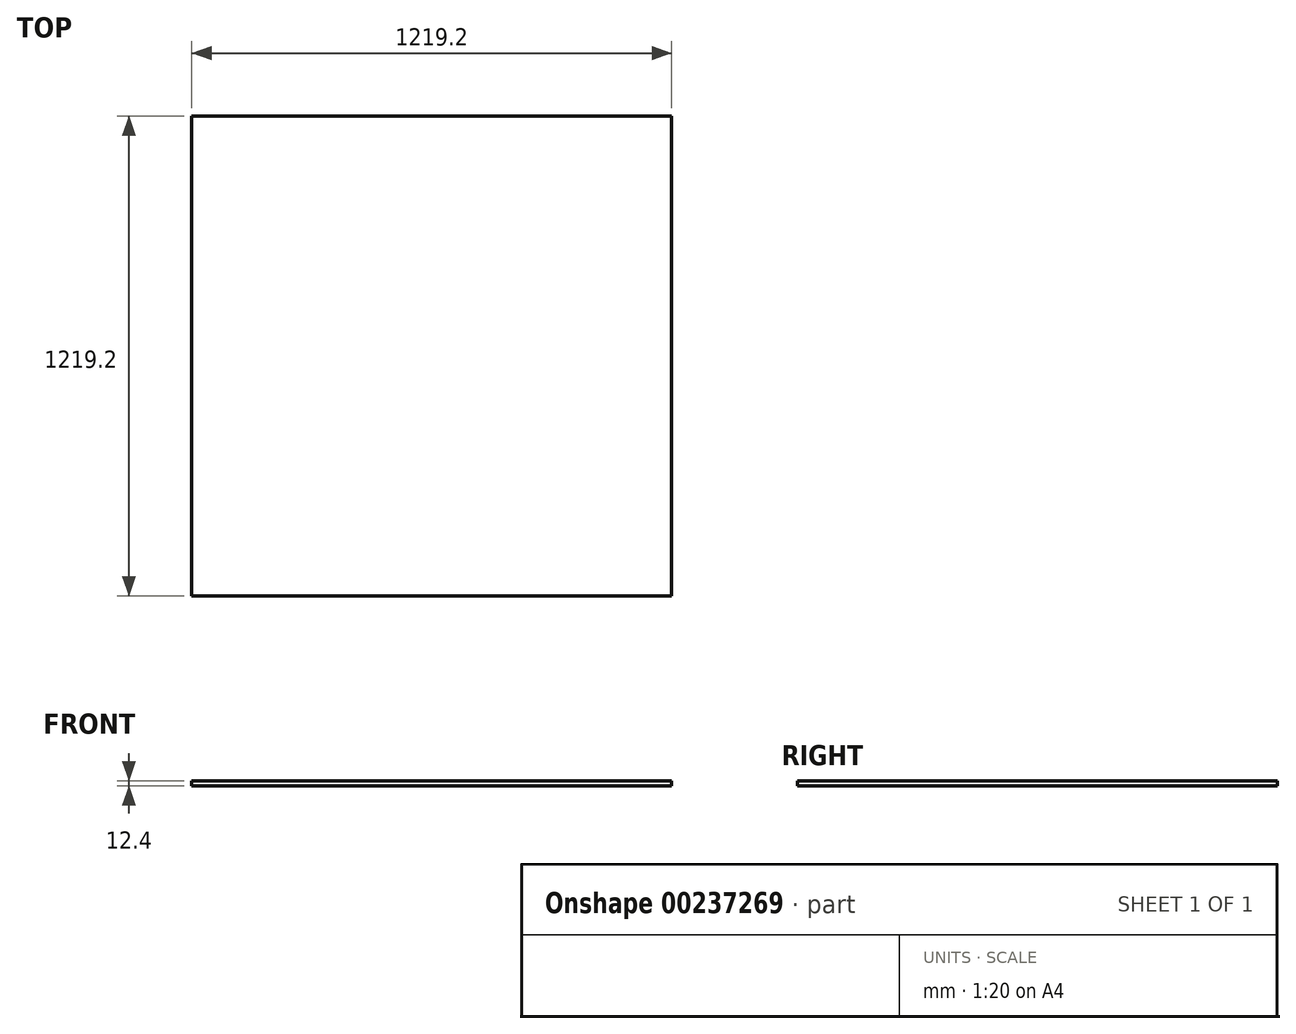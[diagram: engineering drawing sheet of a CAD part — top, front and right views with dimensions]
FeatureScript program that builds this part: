
annotation { "Feature Type Name" : "Feature", "Feature Type Description" : "" }
export const myFeature = defineFeature(function(context is Context, id is Id, definition is map)
    precondition{}
    {
        {
            var Q0;
            Q0=qCreatedBy(makeId("Top.planeOp"),FACE);
            var sketch = newSketch(context, id + "F0", { "sketchPlane" : qUnion([Q0])});
            skLineSegment(sketch, "E0.bottom", {"start": v(0, 0) * mm, "end": v(1219.2, 0) * mm});
            skLineSegment(sketch, "E0.top", {"start": v(0, 1219.2) * mm, "end": v(1219.2, 1219.2) * mm});
            skLineSegment(sketch, "E0.left", {"start": v(0, 0) * mm, "end": v(0, 1219.2) * mm});
            skLineSegment(sketch, "E0.right", {"start": v(1219.2, 0) * mm, "end": v(1219.2, 1219.2) * mm});
            skSolve(sketch);
        }
        {
            var Q0;
            Q0=makeQuery(id+"F0.imprint","IMPRINT",FACE,{"disambiguationData":[TD([[makeQuery(id+"F0.imprint","IMPRINT",EDGE,{"derivedFrom":sQuery(id+"F0.wireOp",EDGE,"E0.bottom")}),1.0]])]});
            extrude(context, id + "F1", {"entities" : qUnion([Q0]), "depth" : 12.4 * mm});
        }
    });
